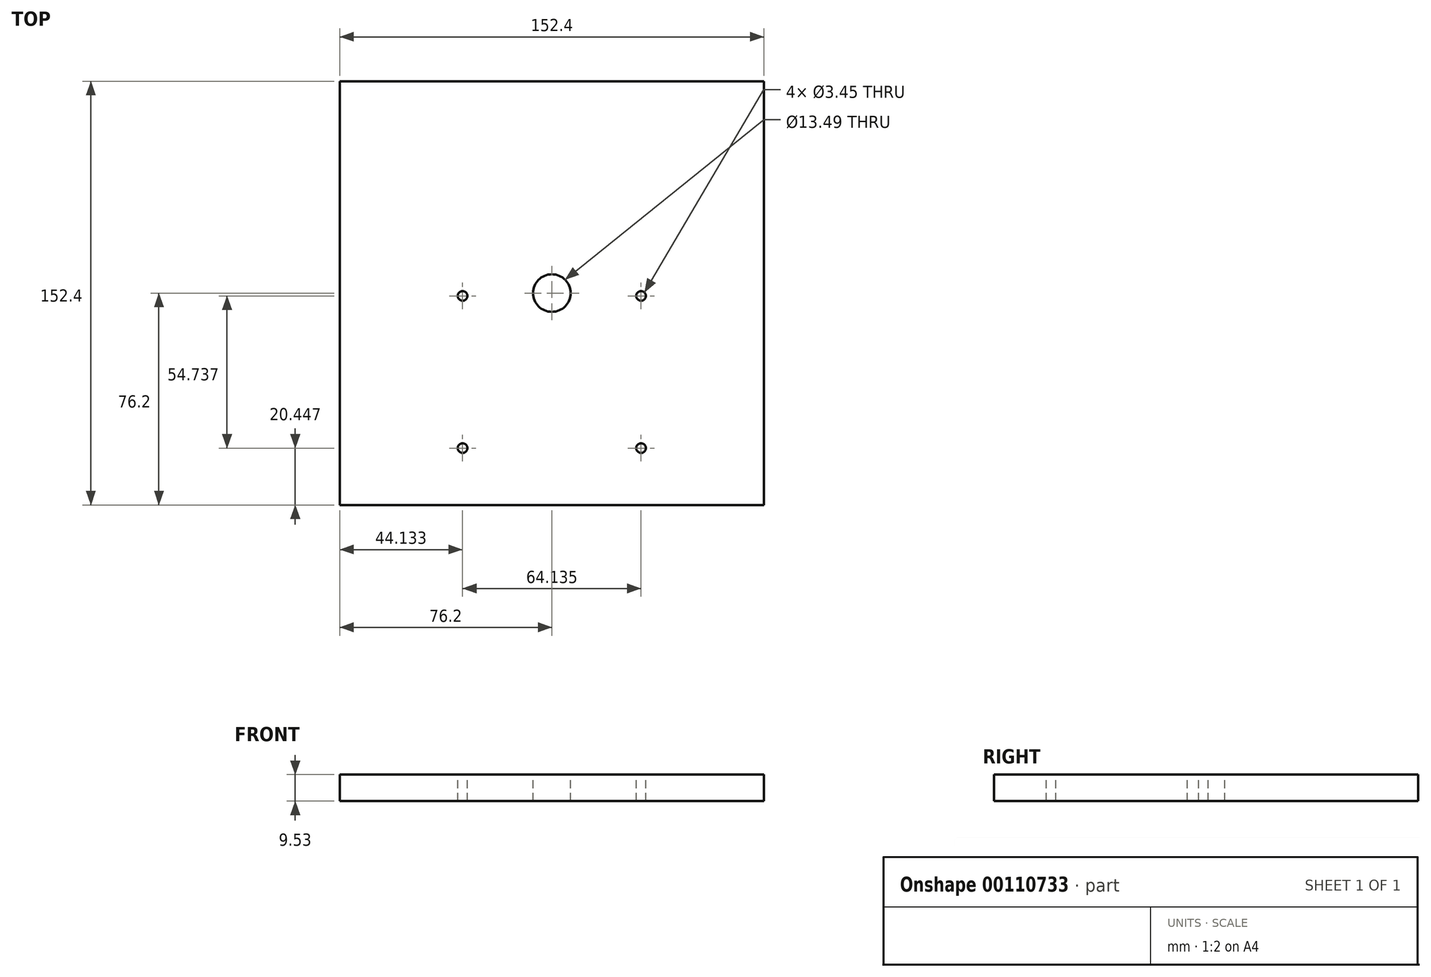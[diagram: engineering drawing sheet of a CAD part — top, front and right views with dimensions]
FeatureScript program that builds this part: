
annotation { "Feature Type Name" : "Feature", "Feature Type Description" : "" }
export const myFeature = defineFeature(function(context is Context, id is Id, definition is map)
    precondition{}
    {
        {
            var Q0;
            Q0=qCreatedBy(makeId("Top.planeOp"),FACE);
            var sketch = newSketch(context, id + "F0", { "sketchPlane" : qUnion([Q0])});
            skLineSegment(sketch, "E0.bottom", {"start": v(-76.2, 76.2) * mm, "end": v(76.2, 76.2) * mm});
            skLineSegment(sketch, "E0.top", {"start": v(-76.2, -76.2) * mm, "end": v(76.2, -76.2) * mm});
            skLineSegment(sketch, "E0.left", {"start": v(-76.2, 76.2) * mm, "end": v(-76.2, -76.2) * mm});
            skLineSegment(sketch, "E0.right", {"start": v(76.2, 76.2) * mm, "end": v(76.2, -76.2) * mm});
            skSolve(sketch);
        }
        {
            var Q0;
            Q0 = qSketchRegion(id + "F0", true);
            extrude(context, id + "F1", {"entities" : qUnion([Q0]), "depth" : 9.52 * mm});
        }
        {
            var Q0;
            Q0=makeQuery(id+"F1.opExtrude","CAP_FACE",FACE,{"disambiguationData":[OSD([sQuery(id+"F0.wireOp",EDGE,"E0.bottom"),sQuery(id+"F0.wireOp",EDGE,"E0.top"),sQuery(id+"F0.wireOp",EDGE,"E0.left"),sQuery(id+"F0.wireOp",EDGE,"E0.right")])],"isStart":false});
            var sketch = newSketch(context, id + "F2", { "sketchPlane" : qUnion([Q0])});
            skPoint(sketch, "E1.middle", {"position": v(0, 0) * mm});
            skCircle(sketch, "E2", {"center": v(0, 0) * mm, "radius": 6.75 * mm});
            skCircle(sketch, "E3", {"center": v(32.07, -1.02) * mm, "radius": 1.78 * mm});
            skCircle(sketch, "E4", {"center": v(-32.07, -1.02) * mm, "radius": 1.78 * mm});
            skCircle(sketch, "E5", {"center": v(-32.07, -55.75) * mm, "radius": 1.78 * mm});
            skCircle(sketch, "E6", {"center": v(32.07, -55.75) * mm, "radius": 1.78 * mm});
            skLineSegment(sketch, "E7", {"start": v(-32.07, -1.02) * mm, "end": v(32.07, -1.02) * mm, "construction": true});
            skPoint(sketch, "E8", {"position": v(0, -1.02) * mm});
            skSolve(sketch);
        }
        {
            var Q0;
            Q0=sQuery(id+"F2.wireOp",VERTEX,"E4.center");
            var Q1;
            Q1=sQuery(id+"F2.wireOp",VERTEX,"E5.center");
            var Q2;
            Q2=sQuery(id+"F2.wireOp",VERTEX,"E6.center");
            var Q3;
            Q3=sQuery(id+"F2.wireOp",VERTEX,"E3.center");
            var Q4;
            Q4=makeQuery(id+"F1.opExtrude","SWEPT_BODY",BODY,{"disambiguationData":[OSD([sQuery(id+"F0.wireOp",EDGE,"E0.bottom"),sQuery(id+"F0.wireOp",EDGE,"E0.top"),sQuery(id+"F0.wireOp",EDGE,"E0.left"),sQuery(id+"F0.wireOp",EDGE,"E0.right")])]});
            hole(context, id + "F3", {"style" : HoleStyle.SIMPLE, "endStyle" : HoleEndStyle.THROUGH, "standardTappedOrClearance" : lookupTablePath({ "standard" : "ANSI", "fit" : "Normal (ASME)", "size" : "#5", "type" : "Clearance" }), "standardBlindInLast" : lookupTablePath({ "fit" : "Free", "standard" : "ANSI", "size" : "#5", "type" : "Clearance" }), "holeDiameter" : 3.45 * mm, "locations" : qUnion([Q0, Q1, Q2, Q3]), "scope" : qUnion([Q4]), "isTappedThrough" : true});
        }
        {
            var Q0;
            Q0=makeQuery(id+"F1.opExtrude","CAP_FACE",FACE,{"disambiguationData":[OSD([sQuery(id+"F0.wireOp",EDGE,"E0.bottom"),sQuery(id+"F0.wireOp",EDGE,"E0.top"),sQuery(id+"F0.wireOp",EDGE,"E0.left"),sQuery(id+"F0.wireOp",EDGE,"E0.right")])],"isStart":false});
            var sketch = newSketch(context, id + "F4", { "sketchPlane" : qUnion([Q0])});
            skPoint(sketch, "E9.middle", {"position": v(0, 0) * mm});
            skCircle(sketch, "E10", {"center": v(0, 0) * mm, "radius": 6.75 * mm});
            skSolve(sketch);
        }
        {
            var Q0;
            Q0=sQuery(id+"F4.wireOp",VERTEX,"E9.middle");
            var Q1;
            Q1=makeQuery(id+"F1.opExtrude","SWEPT_BODY",BODY,{"disambiguationData":[OSD([sQuery(id+"F0.wireOp",EDGE,"E0.bottom"),sQuery(id+"F0.wireOp",EDGE,"E0.top"),sQuery(id+"F0.wireOp",EDGE,"E0.left"),sQuery(id+"F0.wireOp",EDGE,"E0.right")])]});
            hole(context, id + "F5", {"style" : HoleStyle.SIMPLE, "endStyle" : HoleEndStyle.THROUGH, "standardTappedOrClearance" : lookupTablePath({ "standard" : "ANSI", "fit" : "Normal (ASME)", "size" : "1/2", "type" : "Clearance" }), "standardBlindInLast" : lookupTablePath({ "fit" : "Free", "standard" : "ANSI", "size" : "1/2", "type" : "Clearance" }), "holeDiameter" : 13.5 * mm, "locations" : qUnion([Q0]), "scope" : qUnion([Q1]), "isTappedThrough" : true});
        }
    });
